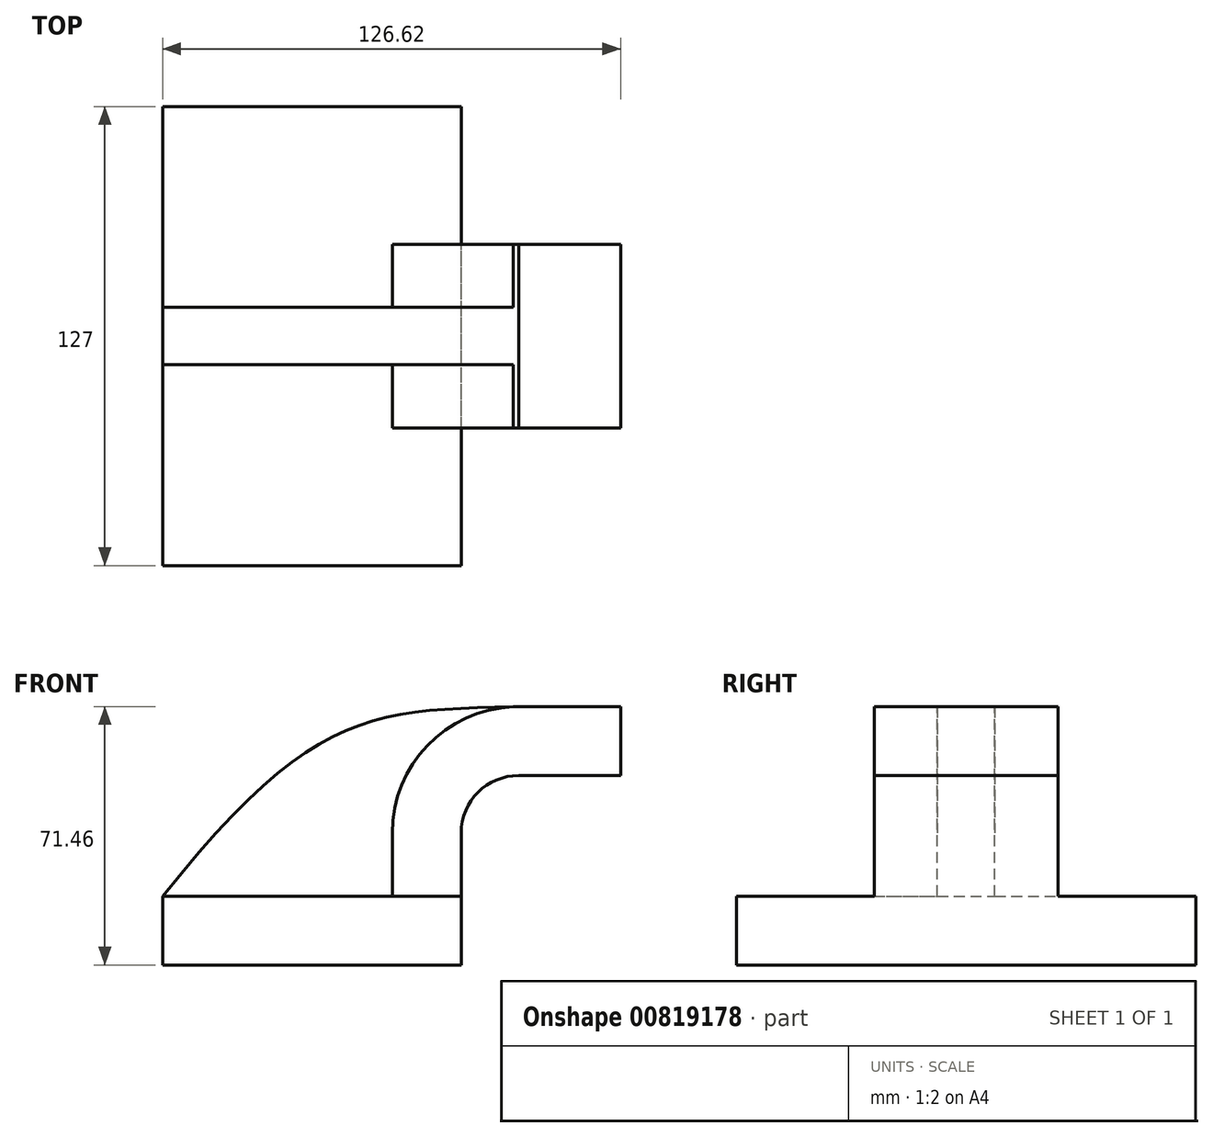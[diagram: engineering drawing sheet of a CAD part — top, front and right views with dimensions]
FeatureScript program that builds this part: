
annotation { "Feature Type Name" : "Feature", "Feature Type Description" : "" }
export const myFeature = defineFeature(function(context is Context, id is Id, definition is map)
    precondition{}
    {
        {
            var Q0;
            Q0=qCreatedBy(makeId("Front.planeOp"),FACE);
            var sketch = newSketch(context, id + "F0", { "sketchPlane" : qUnion([Q0])});
            skLineSegment(sketch, "E0.bottom", {"start": v(41.28, -9.52) * mm, "end": v(-41.28, -9.53) * mm});
            skLineSegment(sketch, "E0.top", {"start": v(41.28, 9.53) * mm, "end": v(-41.28, 9.53) * mm});
            skLineSegment(sketch, "E0.left", {"start": v(41.28, -9.52) * mm, "end": v(41.28, 9.53) * mm});
            skLineSegment(sketch, "E0.right", {"start": v(-41.28, -9.53) * mm, "end": v(-41.28, 9.53) * mm});
            skPoint(sketch, "E0.middle", {"position": v(0, 0) * mm});
            skLineSegment(sketch, "E1.bottom", {"start": v(111.12, 38.1) * mm, "end": v(60.32, 38.1) * mm});
            skLineSegment(sketch, "E1.top", {"start": v(111.12, 66.68) * mm, "end": v(60.32, 66.68) * mm});
            skLineSegment(sketch, "E1.left", {"start": v(111.12, 38.1) * mm, "end": v(111.12, 66.68) * mm});
            skLineSegment(sketch, "E1.right", {"start": v(60.32, 38.1) * mm, "end": v(60.32, 66.67) * mm});
            skPoint(sketch, "E1.middle", {"position": v(85.72, 52.39) * mm});
            skLineSegment(sketch, "E2", {"start": v(41.28, 9.53) * mm, "end": v(41.28, 27) * mm});
            skArc(sketch, "E3", {"start": v(41.27, 27) * mm, "mid": v(45.92, 38.23) * mm, "end": v(57.15, 42.88) * mm});
            skLineSegment(sketch, "E4", {"start": v(57.15, 42.88) * mm, "end": v(85.34, 42.88) * mm});
            skLineSegment(sketch, "E5.0", {"start": v(57.15, 61.93) * mm, "end": v(85.34, 61.93) * mm});
            skArc(sketch, "E5.1", {"start": v(22.23, 27) * mm, "mid": v(32.45, 51.7) * mm, "end": v(57.15, 61.93) * mm});
            skLineSegment(sketch, "E5.2", {"start": v(22.22, 9.53) * mm, "end": v(22.22, 27) * mm});
            skFitSpline(sketch, "E6", {"points": [v(-41.28, 9.53) * mm, v(57.15, 61.93) * mm], "startDerivative": vector(123.83, 154.56) * mm, "endDerivative": vector(122.9, 2.64) * mm});
            skLineSegment(sketch, "E7", {"start": v(85.34, 61.93) * mm, "end": v(85.34, 42.88) * mm});
            skLineSegment(sketch, "E8", {"start": v(85.34, 38.1) * mm, "end": v(85.34, 66.68) * mm});
            skPoint(sketch, "E8.endSnap0", {"position": v(85.72, 66.68) * mm});
            skSolve(sketch);
        }
        {
            var Q0;
            Q0=makeQuery(id+"F0.imprint","IMPRINT",FACE,{"disambiguationData":[TD([[makeQuery(id+"F0.imprint","IMPRINT",EDGE,{"derivedFrom":sQuery(id+"F0.wireOp",EDGE,"E0.bottom")}),-1.0]])]});
            extrude(context, id + "F1", {"entities" : qUnion([Q0]), "depth" : 127 * mm, "offsetDistance" : 25.4 * mm, "symmetric" : true});
        }
        {
            var Q0;
            {var subQ1=sQuery(id+"F0.wireOp",EDGE,"E2");Q0=makeQuery(id+"F0.imprint","IMPRINT",FACE,{"disambiguationData":[TD([[makeQuery(id+"F0.imprint","IMPRINT",EDGE,{"derivedFrom":subQ1}),1.0]])]});}
            var Q1;
            {var subQ5=sQuery(id+"F0.wireOp",EDGE,"E7");Q1=makeQuery(id+"F0.imprint","IMPRINT",FACE,{"disambiguationData":[TD([[makeQuery(id+"F0.imprint","IMPRINT",EDGE,{"derivedFrom":subQ5}),-1.0]])]});}
            extrude(context, id + "F2", {"entities" : qUnion([Q0, Q1]), "operationType" : NewBodyOperationType.ADD, "depth" : 50.8 * mm, "offsetDistance" : 25.4 * mm, "symmetric" : true});
        }
        {
            var Q0;
            {var subQ3=sQuery(id+"F0.wireOp",EDGE,"E5.2");Q0=makeQuery(id+"F0.imprint","IMPRINT",FACE,{"disambiguationData":[TD([[makeQuery(id+"F0.imprint","IMPRINT",EDGE,{"derivedFrom":subQ3}),1.0]])]});}
            extrude(context, id + "F3", {"entities" : qUnion([Q0]), "operationType" : NewBodyOperationType.ADD, "depth" : 15.88 * mm, "offsetDistance" : 25.4 * mm, "symmetric" : true});
        }
    });
